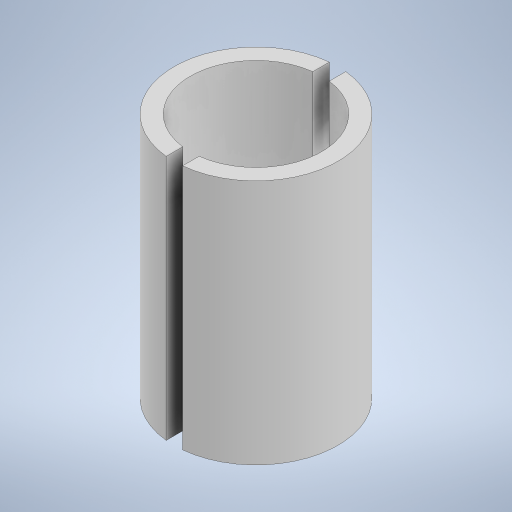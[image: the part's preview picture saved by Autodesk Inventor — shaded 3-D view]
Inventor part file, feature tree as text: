
AUTODESK INVENTOR PART (.ipt)
format: ipt  version: 2023 (Build 270158000, 158)  size: 218,624 bytes
history: native  units: in
note: dims shown in document units (in); Inventor stores cm internally (conversion verified against a paired STEP export)
features: extrude x1, sketch x1
ambient origin geometry x8: Origin, YZ Plane, XZ Plane, XY Plane, X Axis, Y Axis, Z Axis, Center Point
bodies: Solid1 (feature_tree)
feature tree (2):
  extrude  "Extrusion1"  Depth=5.9055in
  sketch  "Sketch1"  dims[d0=3.937in d1=3.1496in d2=0.1969in d3=0.1969in d4=5.9055in d5=0.0in]
